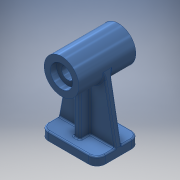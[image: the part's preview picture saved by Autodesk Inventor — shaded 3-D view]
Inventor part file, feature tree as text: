
AUTODESK INVENTOR PART (.ipt)
format: ipt  version: 2016 (Build 200138000, 138)  size: 450,560 bytes
history: native  units: mm
features: extrude x4, sketch x4, projected_geometry x3, hole x1, fillet x1, mirror x1
ambient origin geometry x8: Origin, YZ Plane, XZ Plane, XY Plane, X Axis, Y Axis, Z Axis, Center Point
bodies: Solid1 (feature_tree)
feature tree (14):
  extrude  "Extrusion1"  Depth=82.0mm
  extrude  "Extrusion2"  Depth=12.0mm TaperAngle=0.0deg
  extrude  "Extrusion3"  Depth=100.0mm
  extrude  "Extrusion4"  Depth=2.0mm
  hole  "Hole1"  [1 undecoded]
  fillet  "Fillet1"  Radius=50.0mm
  mirror  "Mirror1"
  sketch  "Sketch1"  dims[d0=12.0mm d2=82.0mm]
  sketch  "Sketch2"  dims[d3=62.0mm d4=12.0mm d5=0.0mm]
  sketch  "Sketch3"  dims[d6=50.0mm d7=100.0mm]
  sketch  "Sketch4"  dims[d8=9.0mm d9=0.0mm d11=38.0mm d12=9.0mm d13=0.0mm d14=50.0mm d16=82.0mm d17=0.0mm d18=10.0mm d19=10.0mm d20=18.0mm d21=6.0mm d22=32.0mm d23=9.0mm d24=90.0deg d25=8.0mm d26=20.594885mm d27=2.0mm]
  projected_geometry  "Projected Loop1"
  projected_geometry  "Projected Loop2"
  projected_geometry  "Projected Loop3"
note: 1 required parameter value undecoded (feature->parameter linkage not recoverable at this tier; creation-order binding heuristic only, values carry confidence <= 0.55)
